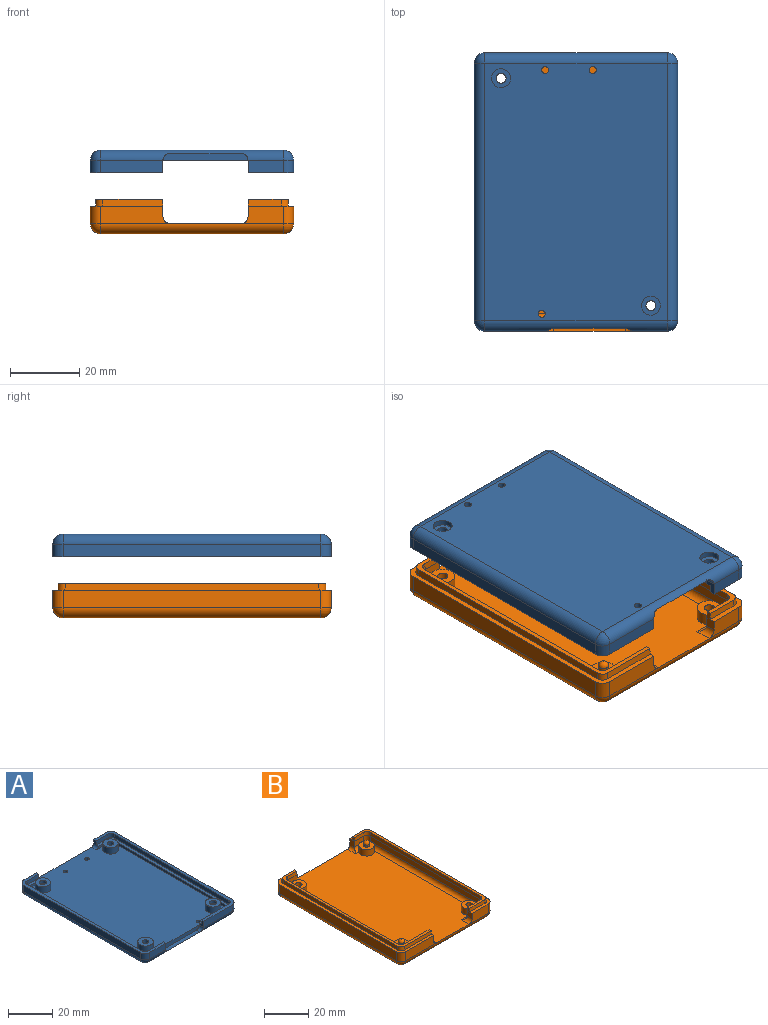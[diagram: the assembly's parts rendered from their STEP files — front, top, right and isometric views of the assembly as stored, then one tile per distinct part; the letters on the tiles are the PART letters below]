
ASSEMBLY  parts=2 mates=1
PART A: 71 faces, bbox 58.8x80.5x6.5 mm
  f0: cylinder r=1.45mm len=4.9mm, axis (0,0,1), area 44.6mm2, adj f21,f69
  f1: cylinder r=1.45mm len=4.9mm, axis (0,0,1), area 44.6mm2, adj f25,f67
  f2: plane 10.2x3.5mm, normal (0,-1,0), area 35.7mm2, adj f5,f6,f49,f50
  f3: plane 9.5x3.5mm, normal (0,1,0), area 28.5mm2, adj f4,f7,f52,f56,f64
  f4: plane 2x1.5mm, normal (-1,0,0), area 3mm2, adj f3,f7,f36,f64
  f5: plane 3.5x3mm, normal (1,0,0), area 7.2mm2, adj f2,f6,f8,f42,f43,f66
  f6: plane 80.5x13.2mm, normal (0,0,1), area 150.4mm2, adj f2,f5,f10,f11,f32,f40,f41,f42
  f7: plane 80.5x21mm, normal (0,0,1), area 162.1mm2, adj f3,f4,f12,f13,f33,f36,f37,f38
  f8: plane 10.2x1.3mm, normal (0,1,0), area 13.3mm2, adj f5,f16,f19,f43
  f9: plane 9.5x1.3mm, normal (0,-1,0), area 10.9mm2, adj f16,f19,f43,f63
  f10: plane 9.5x3.5mm, normal (0,1,0), area 28.5mm2, adj f6,f32,f56,f58,f63
  f11: plane 74.5x3.5mm, normal (-1,0,0), area 260.8mm2, adj f6,f49,f55,f58
  f12: plane 18x3.5mm, normal (0,-1,0), area 63mm2, adj f7,f33,f47,f50
  f13: plane 74.5x3.5mm, normal (1,0,0), area 260.7mm2, adj f7,f47,f51,f52
  f14: plane 74.5x52.8mm, normal (0,0,-1), area 3876.7mm2, adj f44,f45,f46,f50,f51,f55,f56,f68
  f15: plane 9.5x1.3mm, normal (0,-1,0), area 10.9mm2, adj f18,f19,f39,f64
  f16: plane 74.5x1.3mm, normal (1,0,0), area 96.8mm2, adj f8,f9,f19,f43
  f17: plane 18x1.3mm, normal (0,1,0), area 23.4mm2, adj f18,f19,f33,f39
  f18: plane 74.5x1.3mm, normal (-1,0,0), area 96.8mm2, adj f15,f17,f19,f39
  f19: plane 77.5x52.8mm, normal (0,0,1), area 3871.6mm2, adj f8,f9,f15,f16,f17,f18,f20,f22
  f20: cylinder r=3.5mm len=7mm, axis (0,0,-1), area 77mm2, adj f19,f21
  f21: plane 7x7mm, normal (0,0,1), area 31.9mm2, adj f0,f20
  f22: cylinder r=3.5mm len=7mm, axis (0,0,-1), area 77mm2, adj f19,f23
  f23: plane 7x7mm, normal (0,0,1), area 30.4mm2, adj f22,f30
  f24: cylinder r=3.5mm len=7mm, axis (0,0,-1), area 77mm2, adj f19,f25
  f25: plane 7x7mm, normal (0,0,1), area 31.9mm2, adj f1,f24
  f26: cylinder r=3.5mm len=7mm, axis (0,0,-1), area 77mm2, adj f19,f27
  f27: plane 7x7mm, normal (0,0,1), area 30.4mm2, adj f26,f28
  f28: cylinder r=1.6mm len=3.2mm, axis (0,0,1), area 16.1mm2, adj f27,f29
  f29: plane 3.2x3.2mm, normal (0,0,1), area 8mm2, adj f28
  f30: cylinder r=1.6mm len=3.2mm, axis (0,0,1), area 16.1mm2, adj f23,f31
  f31: plane 3.2x3.2mm, normal (0,0,1), area 8mm2, adj f30
  f32: plane 2x1.5mm, normal (1,0,0), area 3mm2, adj f6,f10,f40,f63
  f33: plane 3.5x3mm, normal (-1,0,0), area 7.2mm2, adj f7,f12,f17,f37,f39,f65
  f34: plane 24.6x2mm, normal (0,-1,0), area 47.5mm2, adj f19,f35,f65,f66
  f35: plane 20.6x2.24mm, normal (0,0,1), area 46.1mm2, adj f34,f50,f65,f66
  f36: plane 7.51x2.2mm, normal (0,-1,0), area 16.5mm2, adj f4,f7,f39,f62,f64
  f37: plane 17.5x2.2mm, normal (0,1,0), area 38.5mm2, adj f7,f33,f39,f61
  f38: plane 73.5x2.2mm, normal (-1,0,0), area 161.7mm2, adj f7,f39,f61,f62
  f39: plane 77.5x19.5mm, normal (0,0,1), area 153.6mm2, adj f15,f17,f18,f33,f36,f37,f38,f61
  f40: plane 7.51x2.2mm, normal (0,-1,0), area 16.5mm2, adj f6,f32,f43,f59,f63
  f41: plane 73.5x2.2mm, normal (1,0,0), area 161.7mm2, adj f6,f43,f59,f60
  f42: plane 9.7x2.2mm, normal (0,1,0), area 21.3mm2, adj f5,f6,f43,f60
  f43: plane 77.5x11.7mm, normal (0,0,1), area 141.9mm2, adj f5,f8,f9,f16,f40,f41,f42,f59
  f44: cylinder r=1mm len=3mm, axis (0,0,-1), area 18.8mm2, adj f14,f19
  f45: cylinder r=1mm len=3mm, axis (0,0,-1), area 18.8mm2, adj f14,f19
  f46: cylinder r=1mm len=3mm, axis (0,0,-1), area 18.8mm2, adj f14,f19
  f47: cylinder r=3mm len=3.5mm, axis (0,0,-1), area 16.5mm2, adj f7,f12,f13,f48
  f48: sphere r=3mm, area 14.1mm2, adj f47,f50,f51
  f49: cylinder r=3mm len=3.5mm, axis (0,0,1), area 16.5mm2, adj f2,f6,f11,f53
  f50: cylinder r=3mm len=52.8mm, axis (1,0,0), area 197mm2, adj f2,f12,f14,f35,f48,f53,f65,f66
  f51: cylinder r=3mm len=74.5mm, axis (0,1,0), area 351.1mm2, adj f13,f14,f48,f54
  f52: cylinder r=3mm len=3.5mm, axis (0,0,1), area 16.5mm2, adj f3,f7,f13,f54
  f53: sphere r=3mm, area 14.1mm2, adj f49,f50,f55
  f54: sphere r=3mm, area 14.1mm2, adj f51,f52,f56
  f55: cylinder r=3mm len=74.5mm, axis (0,-1,0), area 351.1mm2, adj f11,f14,f53,f57
  f56: cylinder r=3mm len=52.8mm, axis (-1,0,0), area 248.8mm2, adj f3,f10,f14,f19,f54,f57
  f57: sphere r=3mm, area 14.1mm2, adj f55,f56,f58
  f58: cylinder r=3mm len=3.5mm, axis (0,0,-1), area 16.5mm2, adj f6,f10,f11,f57
  f59: cylinder r=2mm len=2.2mm, axis (0,0,-1), area 6.9mm2, adj f6,f40,f41,f43
  f60: cylinder r=2mm len=2.2mm, axis (0,0,-1), area 6.9mm2, adj f6,f41,f42,f43
  f61: cylinder r=2mm len=2.2mm, axis (0,0,-1), area 6.9mm2, adj f7,f37,f38,f39
  f62: cylinder r=2mm len=2.2mm, axis (0,0,-1), area 6.9mm2, adj f7,f36,f38,f39
  f63: cylinder r=1.5mm len=3mm, axis (0,-1,0), area 6.8mm2, adj f9,f10,f19,f32,f40,f43
  f64: cylinder r=1.5mm len=3mm, axis (0,1,0), area 6.8mm2, adj f3,f4,f15,f19,f36,f39
  f65: cylinder r=2mm len=3mm, axis (0,1,0), area 8.3mm2, adj f33,f34,f35,f50
  f66: cylinder r=2mm len=3mm, axis (0,-1,0), area 8.3mm2, adj f5,f34,f35,f50
  f67: plane 5.5x5.5mm, normal (0,0,-1), area 17.2mm2, adj f1,f68
  f68: cylinder r=2.75mm len=5.5mm, axis (0,0,-1), area 27.6mm2, adj f14,f67
  f69: plane 5.5x5.5mm, normal (0,0,-1), area 17.2mm2, adj f0,f70
  f70: cylinder r=2.75mm len=5.5mm, axis (0,0,-1), area 27.6mm2, adj f14,f69
PART B: 100 faces, bbox 58.9x80.6x10.1 mm
  f0: cylinder r=1.45mm len=4.9mm, axis (0,0,1), area 44.6mm2, adj f29,f66
  f1: cylinder r=1.45mm len=4.9mm, axis (0,0,1), area 44.6mm2, adj f25,f64
  f2: plane 80.5x48.8mm, normal (0,0,1), area 3583.3mm2, adj f22,f24,f26,f28,f37,f43,f46,f49
  f3: plane 0.21x0.18mm, normal (0,0,1), area 0mm2, adj f22,f53,f57
  f4: plane 0.21x0.18mm, normal (0,0,1), area 0mm2, adj f24,f56,f57
  f5: plane 0.21x0.18mm, normal (0,0,1), area 0mm2, adj f28,f49,f52
  f6: plane 20x5mm, normal (0,-1,0), area 90.9mm2, adj f8,f33,f36,f37,f63
  f7: plane 9.5x5mm, normal (0,1,0), area 40.5mm2, adj f10,f30,f39,f43,f61
  f8: plane 80.59x21.09mm, normal (0,0,1), area 162.1mm2, adj f6,f12,f13,f31,f33,f36,f45,f87
  f9: plane 16x3mm, normal (0,1,0), area 48mm2, adj f33,f53,f54,f91
  f10: plane 80.59x13.29mm, normal (0,0,1), area 150.4mm2, adj f7,f14,f15,f30,f32,f34,f39,f74
  f11: plane 6x3mm, normal (0,-1,0), area 18mm2, adj f31,f56,f59,f93
  f12: plane 9.5x5mm, normal (0,1,0), area 40.5mm2, adj f8,f31,f43,f45,f60
  f13: plane 74.5x5mm, normal (-1,0,0), area 372.5mm2, adj f8,f36,f42,f45
  f14: plane 12.2x5mm, normal (0,-1,0), area 51.9mm2, adj f10,f32,f34,f37,f62
  f15: plane 74.5x5mm, normal (1,0,0), area 372.5mm2, adj f10,f34,f38,f39
  f16: plane 74.5x52.8mm, normal (0,0,-1), area 3886.1mm2, adj f37,f38,f42,f43,f65,f67
  f17: plane 6x3mm, normal (0,-1,0), area 18mm2, adj f30,f46,f47,f76
  f18: plane 70.51x3mm, normal (1,0,0), area 211.5mm2, adj f54,f57,f59,f92
  f19: plane 8.2x3mm, normal (0,1,0), area 24.6mm2, adj f32,f50,f52,f78
  f20: plane 70.51x3mm, normal (-1,0,0), area 211.5mm2, adj f47,f49,f50,f77
  f21: plane 0.21x0.18mm, normal (0,0,1), area 0mm2, adj f26,f46,f49
  f22: cylinder r=3.5mm len=7mm, axis (0,0,-1), area 75.6mm2, adj f2,f3,f23,f53,f57
  f23: plane 7x7mm, normal (0,0,1), area 31.9mm2, adj f22,f71
  f24: cylinder r=3.5mm len=7mm, axis (0,0,-1), area 75.6mm2, adj f2,f4,f25,f56,f57
  f25: plane 7x7mm, normal (0,0,1), area 31.9mm2, adj f1,f24
  f26: cylinder r=3.5mm len=7mm, axis (0,0,-1), area 75.6mm2, adj f2,f21,f27,f46,f49
  f27: plane 7x7mm, normal (0,0,1), area 31.9mm2, adj f26,f68
  f28: cylinder r=3.5mm len=7mm, axis (0,0,-1), area 75.6mm2, adj f2,f5,f29,f49,f52
  f29: plane 7x7mm, normal (0,0,1), area 31.9mm2, adj f0,f28
  f30: plane 3.5x3.06mm, normal (-1,0,0), area 10.5mm2, adj f7,f10,f17,f46,f61,f75
  f31: plane 3.5x3.06mm, normal (1,0,0), area 10.5mm2, adj f8,f11,f12,f56,f60,f94
  f32: plane 3x3mm, normal (-1,0,0), area 9mm2, adj f10,f14,f19,f62,f79
  f33: plane 3x3mm, normal (1,0,0), area 9mm2, adj f6,f8,f9,f63,f90
  f34: cylinder r=3mm len=5mm, axis (0,0,-1), area 23.6mm2, adj f10,f14,f15,f35
  f35: sphere r=3mm, area 14.1mm2, adj f34,f37,f38
  f36: cylinder r=3mm len=5mm, axis (0,0,1), area 23.6mm2, adj f6,f8,f13,f40
  f37: cylinder r=3mm len=52.8mm, axis (1,0,0), area 248.8mm2, adj f2,f6,f14,f16,f35,f40
  f38: cylinder r=3mm len=74.5mm, axis (0,1,0), area 351.1mm2, adj f15,f16,f35,f41
  f39: cylinder r=3mm len=5mm, axis (0,0,1), area 23.6mm2, adj f7,f10,f15,f41
  f40: sphere r=3mm, area 14.1mm2, adj f36,f37,f42
  f41: sphere r=3mm, area 9mm2, adj f38,f39,f43
  f42: cylinder r=3mm len=74.5mm, axis (0,-1,0), area 351.1mm2, adj f13,f16,f40,f44
  f43: cylinder r=3mm len=52.8mm, axis (-1,0,0), area 248.8mm2, adj f2,f7,f12,f16,f41,f44
  f44: sphere r=3mm, area 9mm2, adj f42,f43,f45
  f45: cylinder r=3mm len=5mm, axis (0,0,-1), area 23.6mm2, adj f8,f12,f13,f44
  f46: cylinder r=2mm len=7.5mm, axis (-1,0,0), area 16.2mm2, adj f2,f17,f21,f26,f30,f48,f61
  f47: cylinder r=2mm len=3mm, axis (0,0,1), area 9.4mm2, adj f17,f20,f48,f83
  f48: sphere r=2mm, area 4mm2, adj f46,f47,f49
  f49: cylinder r=2mm len=70.5mm, axis (0,1,0), area 217mm2, adj f2,f5,f20,f21,f26,f28,f48,f51
  f50: cylinder r=2mm len=3mm, axis (0,0,-1), area 9.4mm2, adj f19,f20,f51,f84
  f51: sphere r=2mm, area 6.3mm2, adj f49,f50,f52
  f52: cylinder r=2mm len=10.2mm, axis (1,0,0), area 23.9mm2, adj f2,f5,f19,f28,f51,f62
  f53: cylinder r=2mm len=18mm, axis (1,0,0), area 48.4mm2, adj f2,f3,f9,f22,f55,f63
  f54: cylinder r=2mm len=3mm, axis (0,0,1), area 9.4mm2, adj f9,f18,f55,f96
  f55: sphere r=2mm, area 6.3mm2, adj f53,f54,f57
  f56: cylinder r=2mm len=7.5mm, axis (-1,0,0), area 16.2mm2, adj f2,f4,f11,f24,f31,f58,f60
  f57: cylinder r=2mm len=70.5mm, axis (0,-1,0), area 217mm2, adj f2,f3,f4,f18,f22,f24,f55,f58
  f58: sphere r=2mm, area 8.6mm2, adj f56,f57,f59
  f59: cylinder r=2mm len=3mm, axis (0,0,-1), area 9.4mm2, adj f11,f18,f58,f97
  f60: cylinder r=1.5mm len=5mm, axis (0,-1,0), area 9.5mm2, adj f2,f12,f31,f56
  f61: cylinder r=1.5mm len=5mm, axis (0,1,0), area 9.5mm2, adj f2,f7,f30,f46
  f62: cylinder r=2mm len=5mm, axis (0,1,0), area 12.6mm2, adj f2,f14,f32,f52
  f63: cylinder r=2mm len=5mm, axis (0,-1,0), area 12.6mm2, adj f2,f6,f33,f53
  f64: plane 5.5x5.5mm, normal (0,0,-1), area 17.2mm2, adj f1,f65
  f65: cylinder r=2.75mm len=5.5mm, axis (0,0,-1), area 27.6mm2, adj f16,f64
  f66: plane 5.5x5.5mm, normal (0,0,-1), area 17.2mm2, adj f0,f67
  f67: cylinder r=2.75mm len=5.5mm, axis (0,0,-1), area 27.6mm2, adj f16,f66
  f68: cylinder r=1.45mm len=2.9mm, axis (0,0,-1), area 10mm2, adj f27,f70
  f69: plane 0.1x0.1mm, normal (0,0,1), area 0mm2, adj f70
  f70: torus R=0.05mm, axis (0,0,1), area 13mm2, adj f68,f69
  f71: cylinder r=1.45mm len=2.9mm, axis (0,0,-1), area 10mm2, adj f23,f73
  f72: plane 0.1x0.1mm, normal (0,0,1), area 0mm2, adj f73
  f73: torus R=0.05mm, axis (0,0,1), area 13mm2, adj f71,f72
  f74: plane 7.5x2mm, normal (0,1,0.05), area 14.8mm2, adj f10,f75,f82,f86
  f75: plane 2x1.5mm, normal (-1,0,0.05), area 2.8mm2, adj f30,f74,f76,f82
  f76: plane 6.11x2mm, normal (0,-1,0.05), area 12mm2, adj f17,f75,f82,f83
  f77: plane 70.72x2mm, normal (-1,0,0.05), area 141.4mm2, adj f20,f82,f83,f84
  f78: plane 8.31x2mm, normal (0,1,0.05), area 16.4mm2, adj f19,f79,f82,f84
  f79: plane 2x1.5mm, normal (-1,0,0.05), area 2.8mm2, adj f32,f78,f80,f82
  f80: plane 9.7x2mm, normal (0,-1,0.05), area 19.2mm2, adj f10,f79,f82,f85
  f81: plane 73.51x2mm, normal (1,0,0.05), area 147mm2, adj f10,f82,f85,f86
  f82: plane 77.38x11.58mm, normal (0,0,1), area 123.2mm2, adj f74,f75,f76,f77,f78,f79,f80,f81
  f83: cylinder r=2mm len=2.1mm, axis (0.05,0.05,1), area 6.3mm2, adj f47,f76,f77,f82
  f84: cylinder r=2mm len=2.1mm, axis (0.05,-0.05,1), area 6.3mm2, adj f50,f77,f78,f82
  f85: cylinder r=2mm len=2.1mm, axis (0.05,-0.05,-1), area 6.3mm2, adj f10,f80,f81,f82
  f86: cylinder r=2mm len=2.1mm, axis (0.05,0.05,-1), area 6.3mm2, adj f10,f74,f81,f82
  f87: plane 7.5x2mm, normal (0,1,0.05), area 14.8mm2, adj f8,f94,f95,f98
  f88: plane 73.51x2mm, normal (-1,0,0.05), area 147mm2, adj f8,f95,f98,f99
  f89: plane 17.5x2mm, normal (0,-1,0.05), area 34.8mm2, adj f8,f90,f95,f99
  f90: plane 2x1.5mm, normal (1,0,0.05), area 2.8mm2, adj f33,f89,f91,f95
  f91: plane 16.11x2mm, normal (0,1,0.05), area 32mm2, adj f9,f90,f95,f96
  f92: plane 70.72x2mm, normal (1,0,0.05), area 141.4mm2, adj f18,f95,f96,f97
  f93: plane 6.11x2mm, normal (0,-1,0.05), area 12mm2, adj f11,f94,f95,f97
  f94: plane 2x1.5mm, normal (1,0,0.05), area 2.8mm2, adj f31,f87,f93,f95
  f95: plane 77.38x19.38mm, normal (0,0,1), area 133.3mm2, adj f87,f88,f89,f90,f91,f92,f93,f94
  f96: cylinder r=2mm len=2.1mm, axis (-0.05,-0.05,1), area 6.3mm2, adj f54,f91,f92,f95
  f97: cylinder r=2mm len=2.1mm, axis (-0.05,0.05,1), area 6.3mm2, adj f59,f92,f93,f95
  f98: cylinder r=2mm len=2.1mm, axis (-0.05,0.05,-1), area 6.3mm2, adj f8,f87,f88,f95
  f99: cylinder r=2mm len=2.1mm, axis (-0.05,-0.05,-1), area 6.3mm2, adj f8,f88,f89,f95
PLACE A rot(axis=(0,-1,0),180deg) t=(93.25,-44.95,22.83)mm
PLACE B t=(34.45,-44.95,-1.42)mm
MATE slider B.f1 <-> A.f1  axis (0,0,1) through (42.2,28.17,5.08)mm
